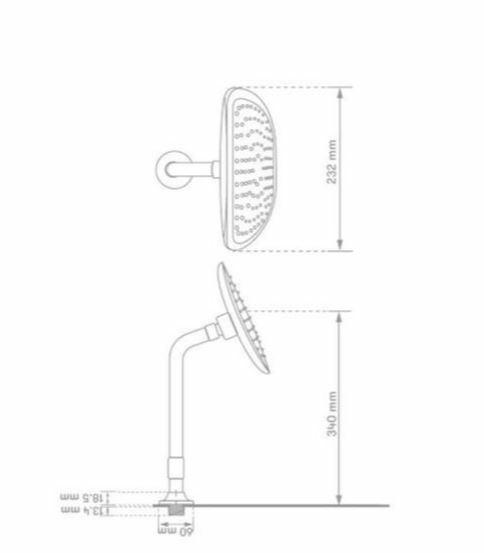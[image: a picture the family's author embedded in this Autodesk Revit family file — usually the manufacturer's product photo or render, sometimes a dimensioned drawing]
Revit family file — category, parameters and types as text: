
# Revit family: 01-1334-11 CONJUNTO REGISTRO DUCHA ATLÁNTICO
name_source: partatom
category: Plumbing Fixtures
revit_build: Autodesk Revit 2018 (Build: 20170223_1515(x64)
units: mm (PartAtom-declared; Revit-internal decimal feet)

## family parameters
Cut with Voids When Loaded = No
Host = Face
OmniClass Number = 23.31.11.00
Part Type = Normal
Room Calculation Point = No
Round Connector Dimension = Use Diameter
Shared = No

## types (1)
- 01-1334-11
    Alto Manija = 85 mm  [stored 0.278871 ft]
    Ancho ducha = 220 mm  [stored 0.721785 ft]
    Ancho manija = 66 mm
    CW Connection = Yes
    Default Elevation = 0 mm  [stored 0 ft]
    Description = Mezclador ducha
    Escudo = 60 mm  [stored 0.19685 ft]
    HW Connection = Yes
    Laton = Laton
    Link Ficha Tecnica = No encontrada en internet
    Manufacturer = Gricol
    Metal Laton Cromado = Metal Laton Cromado
    Model = 01-1334-11
    Plastico - ABS Cromado = Plastico - ABS Cromado
    Product Name = CONJUNTO REGISTRO DUCHA ATLÁNTICO
    Type Image = LOGO-01.jpg
    URL = https://www.gricol.com
    Vent Connection = No
    Waste Connection = No

note: [stored X ft] marks values corroborated as IEEE doubles in the binary element streams (Revit-internal decimal feet)

## geometry (parser evidence)
native form markers: Blend x6, Sweep x26
no freeform markers — native parametric forms only
